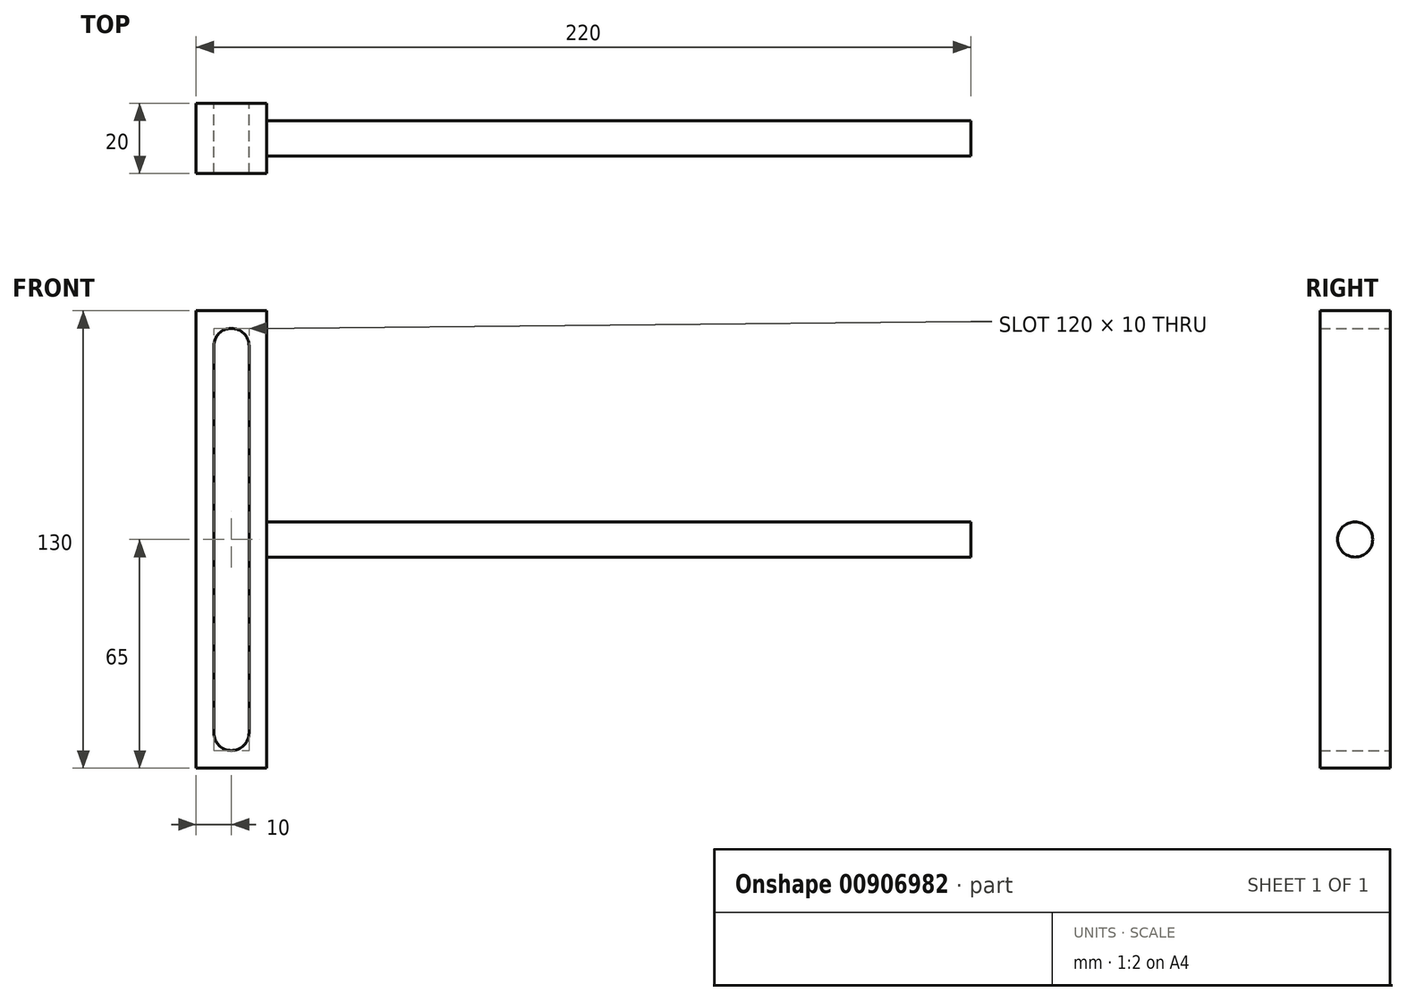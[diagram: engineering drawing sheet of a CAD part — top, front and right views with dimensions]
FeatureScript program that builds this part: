
annotation { "Feature Type Name" : "Feature", "Feature Type Description" : "" }
export const myFeature = defineFeature(function(context is Context, id is Id, definition is map)
    precondition{}
    {
        {
            var Q0;
            Q0=qCreatedBy(makeId("Front.planeOp"),FACE);
            var sketch = newSketch(context, id + "F0", { "sketchPlane" : qUnion([Q0])});
            skLineSegment(sketch, "E0.bottom", {"start": v(-10, 65) * mm, "end": v(10, 65) * mm});
            skLineSegment(sketch, "E0.top", {"start": v(-10, -65) * mm, "end": v(10, -65) * mm});
            skLineSegment(sketch, "E0.left", {"start": v(-10, 65) * mm, "end": v(-10, -65) * mm});
            skLineSegment(sketch, "E0.right", {"start": v(10, 65) * mm, "end": v(10, -65) * mm});
            skLineSegment(sketch, "E1.0", {"start": v(5, 55) * mm, "end": v(5, -55) * mm});
            skLineSegment(sketch, "E2.0", {"start": v(-5, 55) * mm, "end": v(-5, -55) * mm});
            skLineSegment(sketch, "E3.0", {"start": v(0, 60) * mm, "end": v(0, 60) * mm});
            skLineSegment(sketch, "E4.0", {"start": v(0, -60) * mm, "end": v(0, -60) * mm});
            skPoint(sketch, "E5.visualSharp", {"position": v(-5, -60) * mm});
            skArc(sketch, "E5.filletArc", {"start": v(-5, -55) * mm, "mid": v(-3.54, -58.54) * mm, "end": v(0, -60) * mm});
            skPoint(sketch, "E6.visualSharp", {"position": v(5, -60) * mm});
            skArc(sketch, "E6.filletArc", {"start": v(0, -60) * mm, "mid": v(3.54, -58.54) * mm, "end": v(5, -55) * mm});
            skPoint(sketch, "E7.visualSharp", {"position": v(-5, 60) * mm});
            skArc(sketch, "E7.filletArc", {"start": v(0, 60) * mm, "mid": v(-3.54, 58.54) * mm, "end": v(-5, 55) * mm});
            skPoint(sketch, "E8.visualSharp", {"position": v(5, 60) * mm});
            skArc(sketch, "E8.filletArc", {"start": v(5, 55) * mm, "mid": v(3.54, 58.54) * mm, "end": v(0, 60) * mm});
            skSolve(sketch);
        }
        {
            var Q0;
            Q0=makeQuery(id+"F0.imprint","IMPRINT",FACE,{"disambiguationData":[TD([[makeQuery(id+"F0.imprint","IMPRINT",EDGE,{"derivedFrom":sQuery(id+"F0.wireOp",EDGE,"E0.bottom")}),-1.0]])]});
            extrude(context, id + "F1", {"entities" : qUnion([Q0]), "depth" : 10 * mm, "offsetDistance" : 25 * mm, "hasSecondDirection" : true, "secondDirectionOppositeDirection" : true, "secondDirectionDepth" : 10 * mm});
        }
        {
            var Q0;
            Q0=makeQuery(id+"F1.opExtrude","SWEPT_FACE",FACE,{"disambiguationData":[OSD([sQuery(id+"F0.wireOp",EDGE,"E0.right")])]});
            var sketch = newSketch(context, id + "F2", { "sketchPlane" : qUnion([Q0])});
            skCircle(sketch, "E9", {"center": v(0, 0) * mm, "radius": 5 * mm});
            skSolve(sketch);
        }
        {
            var Q0;
            Q0 = qSketchRegion(id + "F2", true);
            extrude(context, id + "F3", {"entities" : qUnion([Q0]), "operationType" : NewBodyOperationType.ADD, "depth" : 200 * mm, "offsetDistance" : 25 * mm});
        }
    });
